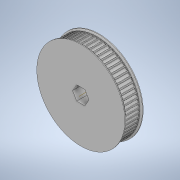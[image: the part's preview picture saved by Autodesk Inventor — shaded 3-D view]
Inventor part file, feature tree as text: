
AUTODESK INVENTOR PART (.ipt)
format: ipt  version: 2022.3 (Build 263350000, 350)  size: 518,144 bytes
history: native  units: in
note: dims shown in document units (in); Inventor stores cm internally (conversion verified against a paired STEP export)
features: sketch x7, extrude x6, mirror x2, chamfer x2, other x1, fillet x1, pattern_circular x1
ambient origin geometry x8: Origin, YZ Plane, XZ Plane, XY Plane, X Axis, Y Axis, Z Axis, Center Point
bodies: Solid1 (feature_tree)
feature tree (20):
  other  "Hex Bore"
  extrude  "HTD Base"  Depth=0.3937in TaperAngle=0.0deg
  extrude  "HTD Flange"  Depth=0.0591in
  mirror  "HTD Flanges"
  chamfer  "HTD Flange Chamfer"  Distance=0.0787in Angle=45.0deg
  extrude  "GT2 Base"  TaperAngle=0.0deg  [1 undecoded]
  extrude  "GT2 Base Tooth"  TaperAngle=0.0deg  [1 undecoded]
  fillet  "GT2 Base Tooth pt. 2"  Radius=2.3761in
  pattern_circular  "GT2 Teeth"  [2 undecoded]
  extrude  "GT2 Flange"  Depth=0.0591in
  mirror  "GT2 Flanges"
  chamfer  "GT2 Flange Chamfer"  Distance=0.0075in
  extrude  "Circle Bore"  TaperAngle=0.0deg  [1 undecoded]
  sketch  "Sketch1"  dims[d0=3.9652in d1=0.3937in d2=0.0in]
  sketch  "Sketch3"  dims[d12=0.0394in d13=0.0591in]
  sketch  "Sketch4"  dims[d14=0.0in]
  sketch  "Sketch5"  dims[d15=0.0394in d16=0.0787in d17=45.0deg]
  sketch  "Sketch6"  dims[d18=0.395in d19=0.0in d20=0.0in]
  sketch  "Sketch7"  dims[d21=0.395in d22=0.0in d23=0.0in d24=2.3761in]
  sketch  "Sketch8"  dims[d25=0.3937in d26=0.0in d27=0.0727in d28=0.0075in d29=0.0in d30=0.0in d31=0.0118in d32=25.1969in d33=360.0deg d35=0.0394in d36=0.0591in d37=0.0in d38=0.0394in d39=0.0787in d40=45.0deg]
note: 5 required parameter values undecoded (feature->parameter linkage not recoverable at this tier; creation-order binding heuristic only, values carry confidence <= 0.55)
